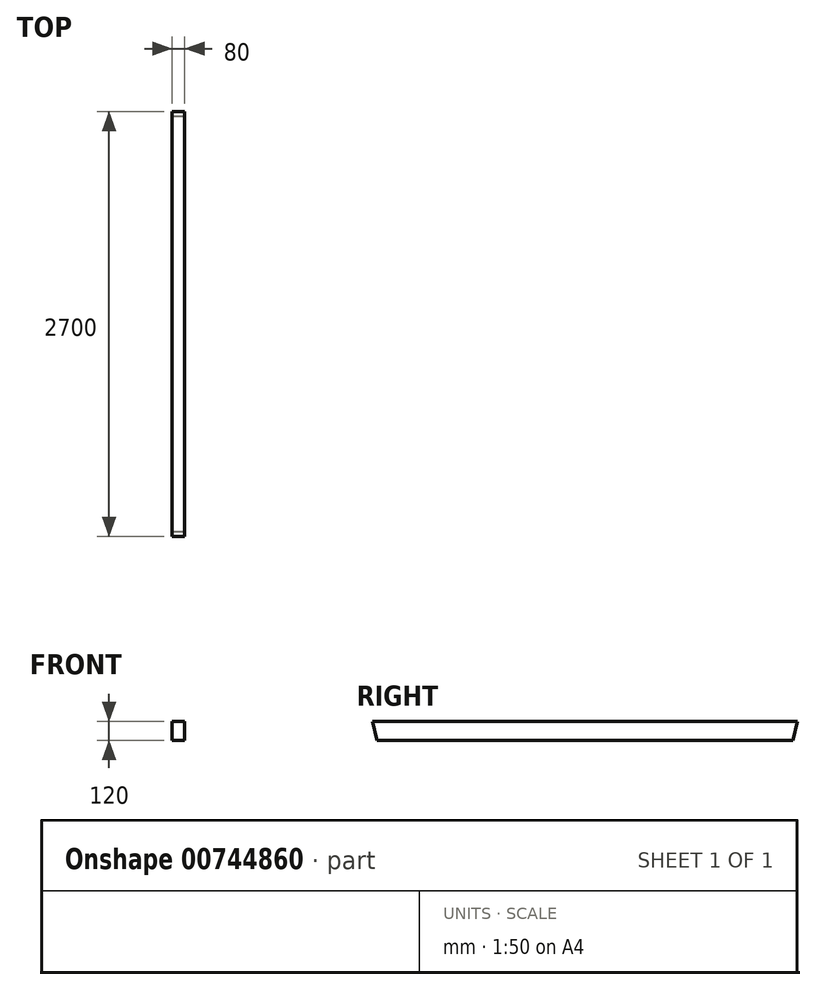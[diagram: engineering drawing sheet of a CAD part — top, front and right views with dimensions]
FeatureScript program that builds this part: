
annotation { "Feature Type Name" : "Feature", "Feature Type Description" : "" }
export const myFeature = defineFeature(function(context is Context, id is Id, definition is map)
    precondition{}
    {
        {
            var Q0;
            Q0=qCreatedBy(makeId("Front.planeOp"),FACE);
            var sketch = newSketch(context, id + "F0", { "sketchPlane" : qUnion([Q0])});
            skLineSegment(sketch, "E0.bottom", {"start": v(0, 0) * mm, "end": v(80, 0) * mm});
            skLineSegment(sketch, "E0.top", {"start": v(0, 120) * mm, "end": v(80, 120) * mm});
            skLineSegment(sketch, "E0.left", {"start": v(0, 0) * mm, "end": v(0, 120) * mm});
            skLineSegment(sketch, "E0.right", {"start": v(80, 0) * mm, "end": v(80, 120) * mm});
            skSolve(sketch);
        }
        {
            var Q0;
            Q0=makeQuery(id+"F0.imprint","IMPRINT",FACE,{"disambiguationData":[TD([[makeQuery(id+"F0.imprint","IMPRINT",EDGE,{"derivedFrom":sQuery(id+"F0.wireOp",EDGE,"E0.bottom")}),1.0]])]});
            extrude(context, id + "F1", {"entities" : qUnion([Q0]), "oppositeDirection" : true, "depth" : 2700 * mm, "offsetDistance" : 25 * mm});
        }
        {
            var Q0;
            Q0=makeQuery(id+"F1.opExtrude","CAP_EDGE",EDGE,{"disambiguationData":[OSD([sQuery(id+"F0.wireOp",EDGE,"E0.bottom")])],"isStart":true});
            chamfer(context, id + "F2", {"entities" : qUnion([Q0]), "chamferType" : ChamferType.TWO_OFFSETS, "width1" : 120 * mm, "oppositeDirection" : false, "width2" : 30 * mm, "tangentPropagation" : true});
        }
        {
            var Q0;
            Q0=makeQuery(id+"F1.opExtrude","CAP_EDGE",EDGE,{"disambiguationData":[OSD([sQuery(id+"F0.wireOp",EDGE,"E0.bottom")])],"isStart":false});
            chamfer(context, id + "F3", {"entities" : qUnion([Q0]), "chamferType" : ChamferType.TWO_OFFSETS, "width1" : 30 * mm, "oppositeDirection" : false, "width2" : 120 * mm, "tangentPropagation" : true});
        }
    });
